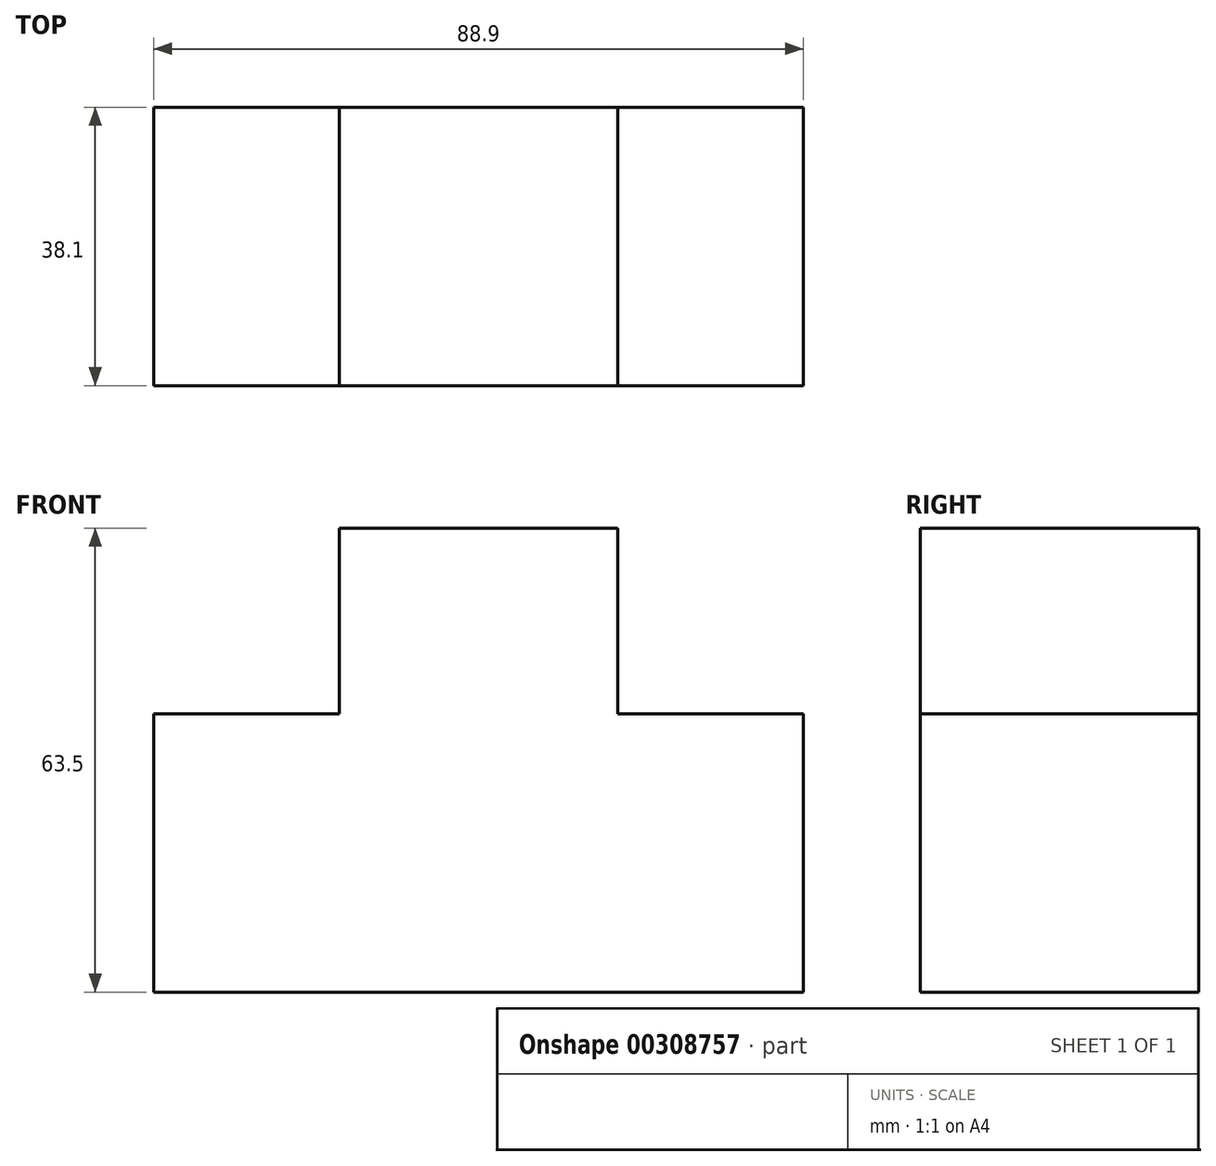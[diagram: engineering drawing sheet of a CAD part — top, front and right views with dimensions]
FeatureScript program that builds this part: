
annotation { "Feature Type Name" : "Feature", "Feature Type Description" : "" }
export const myFeature = defineFeature(function(context is Context, id is Id, definition is map)
    precondition{}
    {
        {
            var Q0;
            Q0=qCreatedBy(makeId("Front.planeOp"),FACE);
            var sketch = newSketch(context, id + "F0", { "sketchPlane" : qUnion([Q0])});
            skLineSegment(sketch, "E0", {"start": v(-43.01, -58.25) * mm, "end": v(45.89, -58.25) * mm});
            skLineSegment(sketch, "E1", {"start": v(45.89, -58.25) * mm, "end": v(45.89, -20.15) * mm});
            skLineSegment(sketch, "E2", {"start": v(45.89, -20.15) * mm, "end": v(20.49, -20.15) * mm});
            skLineSegment(sketch, "E3", {"start": v(20.49, -20.15) * mm, "end": v(20.49, 5.25) * mm});
            skLineSegment(sketch, "E4", {"start": v(20.49, 5.25) * mm, "end": v(-17.61, 5.25) * mm});
            skLineSegment(sketch, "E5", {"start": v(-17.61, 5.25) * mm, "end": v(-17.61, -20.15) * mm});
            skLineSegment(sketch, "E6", {"start": v(-17.61, -20.15) * mm, "end": v(-43.01, -20.15) * mm});
            skLineSegment(sketch, "E7", {"start": v(-43.01, -20.15) * mm, "end": v(-43.01, -58.25) * mm});
            skSolve(sketch);
        }
        {
            var Q0;
            Q0=makeQuery(id+"F0.imprint","IMPRINT",FACE,{"disambiguationData":[TD([[makeQuery(id+"F0.imprint","IMPRINT",EDGE,{"derivedFrom":sQuery(id+"F0.wireOp",EDGE,"E0")}),1.0]])]});
            extrude(context, id + "F1", {"entities" : qUnion([Q0]), "depth" : 38.1 * mm});
        }
    });
